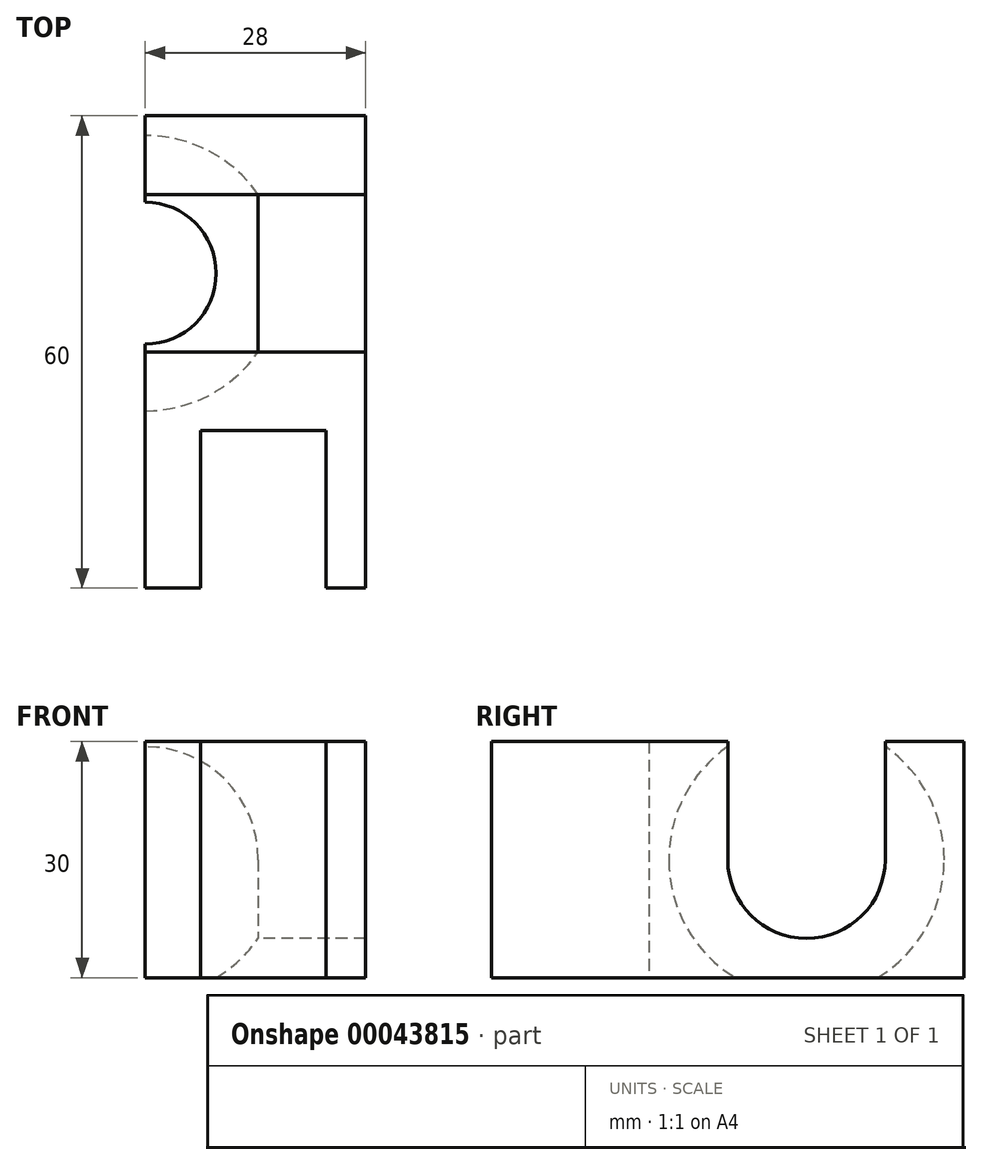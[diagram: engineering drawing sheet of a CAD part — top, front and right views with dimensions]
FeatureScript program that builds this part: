
annotation { "Feature Type Name" : "Feature", "Feature Type Description" : "" }
export const myFeature = defineFeature(function(context is Context, id is Id, definition is map)
    precondition{}
    {
        {
            var Q0;
            Q0=qCreatedBy(makeId("Top.planeOp"),FACE);
            var sketch = newSketch(context, id + "F0", { "sketchPlane" : qUnion([Q0])});
            skLineSegment(sketch, "E0", {"start": v(0, 0) * mm, "end": v(7, 0) * mm});
            skLineSegment(sketch, "E1", {"start": v(7, 0) * mm, "end": v(7, 20) * mm});
            skLineSegment(sketch, "E2", {"start": v(7, 20) * mm, "end": v(23, 20) * mm});
            skLineSegment(sketch, "E3", {"start": v(23, 20) * mm, "end": v(23, 0) * mm});
            skLineSegment(sketch, "E4", {"start": v(23, 0) * mm, "end": v(28, 0) * mm});
            skLineSegment(sketch, "E5", {"start": v(28, 0) * mm, "end": v(28, 60) * mm});
            skLineSegment(sketch, "E6", {"start": v(28, 60) * mm, "end": v(0, 60) * mm});
            skLineSegment(sketch, "E7", {"start": v(0, 60) * mm, "end": v(0, -1.84) * mm});
            skSolve(sketch);
        }
        {
            var Q0;
            Q0 = qSketchRegion(id + "F0", true);
            extrude(context, id + "F1", {"entities" : qUnion([Q0]), "depth" : 30 * mm});
        }
        {
            var Q0;
            Q0=makeQuery(id+"F1.opExtrude","SWEPT_FACE",FACE,{"disambiguationData":[OSD([sQuery(id+"F0.wireOp",EDGE,"E7")])]});
            var sketch = newSketch(context, id + "F2", { "sketchPlane" : qUnion([Q0])});
            skLineSegment(sketch, "E8.0", {"start": v(-20, 30) * mm, "end": v(-20, 0) * mm});
            skLineSegment(sketch, "E9", {"start": v(-20, 30) * mm, "end": v(-60, 0) * mm, "construction": true});
            skCircle(sketch, "E10", {"center": v(-40, 15) * mm, "radius": 10 * mm});
            skLineSegment(sketch, "E11", {"start": v(-50, 15) * mm, "end": v(-50, 30) * mm});
            skLineSegment(sketch, "E12", {"start": v(-30, 15) * mm, "end": v(-30, 30) * mm});
            skLineSegment(sketch, "E13", {"start": v(-60, 15) * mm, "end": v(-20, 15) * mm, "construction": true});
            skArc(sketch, "E14", {"start": v(-57.5, 15) * mm, "mid": v(-40, -2.5) * mm, "end": v(-22.5, 15) * mm});
            skLineSegment(sketch, "E15", {"start": v(-57.5, 15) * mm, "end": v(-22.5, 15) * mm});
            skSolve(sketch);
        }
        {
            var Q0;
            {var subQ0=sQuery(id+"F2.wireOp",EDGE,"E15");var subQ1=sQuery(id+"F2.wireOp",EDGE,"E10");var subQ3=makeQuery(id+"F2.imprint","INTERSECT",VERTEX,{"derivedFrom":[subQ1,sQuery(id+"F2.wireOp",EDGE,"E11"),subQ0]});Q0=makeQuery(id+"F2.imprint","IMPRINT",FACE,{"disambiguationData":[TD([[makeQuery(id+"F2.imprint","IMPRINT",EDGE,{"disambiguationData":[TD([[subQ3,-1.0]])],"derivedFrom":subQ1}),1.0]])]});}
            var Q1;
            {var subQ0=sQuery(id+"F2.wireOp",EDGE,"E15");var subQ1=sQuery(id+"F2.wireOp",EDGE,"E10");var subQ3=makeQuery(id+"F2.imprint","INTERSECT",VERTEX,{"derivedFrom":[subQ1,sQuery(id+"F2.wireOp",EDGE,"E11"),subQ0]});Q1=makeQuery(id+"F2.imprint","IMPRINT",FACE,{"disambiguationData":[TD([[makeQuery(id+"F2.imprint","IMPRINT",EDGE,{"disambiguationData":[TD([[subQ3,1.0]])],"derivedFrom":subQ1}),1.0]])]});}
            var Q2;
            {var subQ2=sQuery(id+"F2.wireOp",EDGE,"E11");Q2=makeQuery(id+"F2.imprint","IMPRINT",FACE,{"disambiguationData":[TD([[makeQuery(id+"F2.imprint","IMPRINT",EDGE,{"derivedFrom":subQ2}),-1.0]])]});}
            extrude(context, id + "F3", {"entities" : qUnion([Q0, Q1, Q2]), "operationType" : NewBodyOperationType.REMOVE, "endBound" : BoundingType.UP_TO_NEXT, "oppositeDirection" : true, "depth" : 25 * mm});
        }
        {
            var Q0;
            {var subQ0=sQuery(id+"F2.wireOp",EDGE,"E15");var subQ1=sQuery(id+"F2.wireOp",EDGE,"E10");var subQ3=makeQuery(id+"F2.imprint","INTERSECT",VERTEX,{"derivedFrom":[subQ1,sQuery(id+"F2.wireOp",EDGE,"E11"),subQ0]});Q0=makeQuery(id+"F2.imprint","IMPRINT",FACE,{"disambiguationData":[TD([[makeQuery(id+"F2.imprint","IMPRINT",EDGE,{"disambiguationData":[TD([[subQ3,-1.0]])],"derivedFrom":subQ1}),1.0]])]});}
            var Q1;
            {var subQ1=sQuery(id+"F2.wireOp",EDGE,"E14");var subQ4=sQuery(id+"F2.wireOp",EDGE,"E15");var subQ9=makeQuery(id+"F2.imprint","INTERSECT",VERTEX,{"disambiguationData":[OD(0.0)],"derivedFrom":[subQ1,subQ4]});Q1=makeQuery(id+"F2.imprint","IMPRINT",FACE,{"disambiguationData":[TD([[makeQuery(id+"F2.imprint","IMPRINT",EDGE,{"disambiguationData":[TD([[subQ9,-1.0]])],"derivedFrom":subQ1}),1.0]])]});}
            var Q2;
            {var subQ0=makeQuery(id+"F1.opExtrude","CAP_EDGE",EDGE,{"disambiguationData":[OSD([sQuery(id+"F0.wireOp",EDGE,"E7")])],"isStart":true});var subQ1=sQuery(id+"F2.wireOp",EDGE,"E14");var subQ3=makeQuery(id+"F2.imprint","INTERSECT",VERTEX,{"disambiguationData":[OD(0.0)],"derivedFrom":[subQ0,subQ1]});Q2=makeQuery(id+"F2.imprint","IMPRINT",FACE,{"disambiguationData":[TD([[makeQuery(id+"F2.imprint","IMPRINT",EDGE,{"disambiguationData":[TD([[subQ3,-1.0]])],"derivedFrom":subQ1}),1.0]])]});}
            var Q3;
            Q3=sQuery(id+"F2.wireOp",EDGE,"E15");
            revolve(context, id + "F4", {"operationType" : NewBodyOperationType.REMOVE, "entities" : qUnion([Q0, Q1, Q2]), "axis" : qUnion([Q3]), "revolveType" : RevolveType.FULL, "oppositeDirection" : true});
        }
    });
